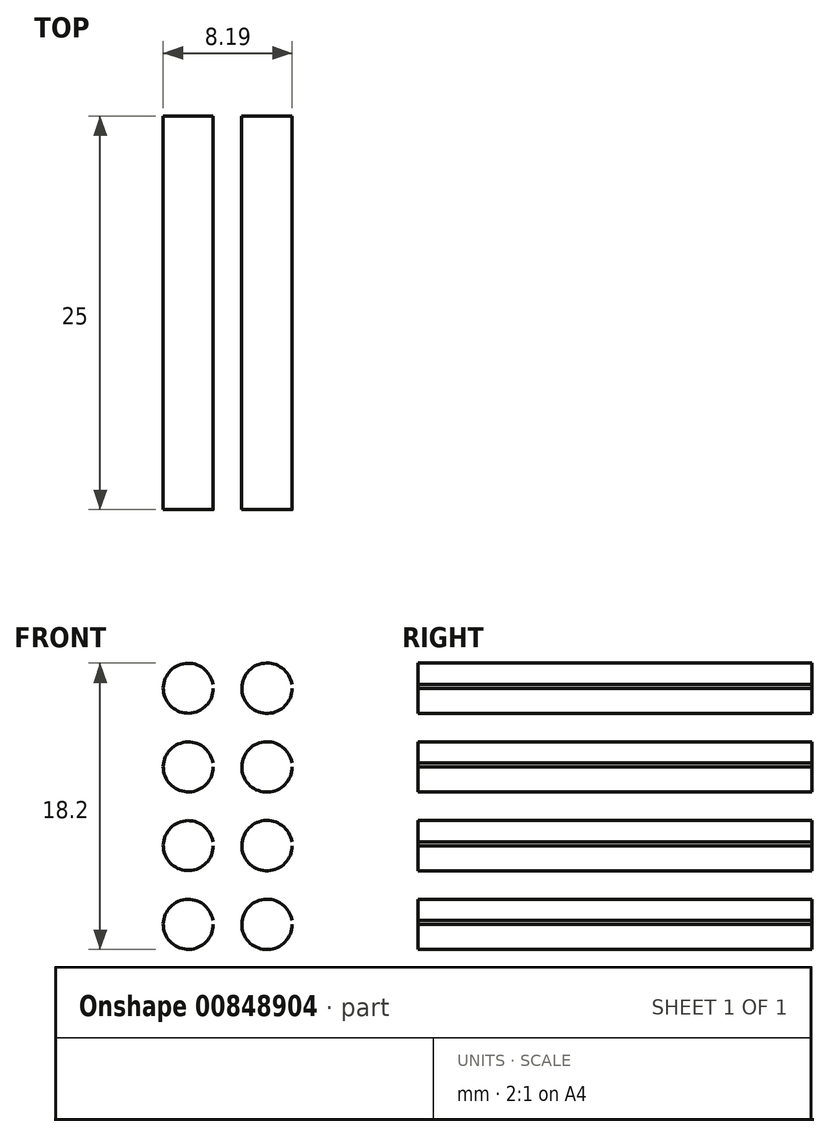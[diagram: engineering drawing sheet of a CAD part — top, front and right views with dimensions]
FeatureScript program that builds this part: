
annotation { "Feature Type Name" : "Feature", "Feature Type Description" : "" }
export const myFeature = defineFeature(function(context is Context, id is Id, definition is map)
    precondition{}
    {
        {
            var Q0;
            Q0=qCreatedBy(makeId("Front.planeOp"),FACE);
            var sketch = newSketch(context, id + "F0", { "sketchPlane" : qUnion([Q0])});
            skArc(sketch, "E0", {"start": v(1.57, 0.25) * mm, "mid": v(-1.58, -0.13) * mm, "end": v(1.59, 0) * mm});
            skLineSegment(sketch, "E1", {"start": v(0, 0) * mm, "end": v(0, 35.3) * mm, "construction": true});
            skLineSegment(sketch, "E2.direction2", {"start": v(0, 0) * mm, "end": v(0, 5) * mm, "construction": true});
            skLineSegment(sketch, "E3", {"start": v(0, 0) * mm, "end": v(0, -5) * mm, "construction": true});
            skLineSegment(sketch, "E4.bottom", {"start": v(0, 0) * mm, "end": v(2, 0) * mm, "construction": true});
            skLineSegment(sketch, "E4.top", {"start": v(0, 0.25) * mm, "end": v(2, 0.25) * mm, "construction": true});
            skLineSegment(sketch, "E4.left", {"start": v(0, 0) * mm, "end": v(0, 0.25) * mm, "construction": true});
            skLineSegment(sketch, "E4.right", {"start": v(2, 0) * mm, "end": v(2, 0.25) * mm, "construction": true});
            skLineSegment(sketch, "E5.0.1.0", {"start": v(0, 5) * mm, "end": v(2, 5) * mm, "construction": true});
            skArc(sketch, "E5.0.1.1", {"start": v(1.57, 5.25) * mm, "mid": v(-1.58, 4.87) * mm, "end": v(1.59, 5) * mm});
            skLineSegment(sketch, "E5.0.1.2", {"start": v(0, 5.25) * mm, "end": v(2, 5.25) * mm, "construction": true});
            skLineSegment(sketch, "E5.0.1.3", {"start": v(2, 5) * mm, "end": v(2, 5.25) * mm, "construction": true});
            skLineSegment(sketch, "E5.0.1.4", {"start": v(0, 5) * mm, "end": v(0, 5.25) * mm, "construction": true});
            skLineSegment(sketch, "E5.0.2.0", {"start": v(0, 10) * mm, "end": v(2, 10) * mm, "construction": true});
            skArc(sketch, "E5.0.2.1", {"start": v(1.57, 10.25) * mm, "mid": v(-1.58, 9.87) * mm, "end": v(1.59, 10) * mm});
            skLineSegment(sketch, "E5.0.2.2", {"start": v(0, 10.25) * mm, "end": v(2, 10.25) * mm, "construction": true});
            skLineSegment(sketch, "E5.0.2.3", {"start": v(2, 10) * mm, "end": v(2, 10.25) * mm, "construction": true});
            skLineSegment(sketch, "E5.0.2.4", {"start": v(0, 10) * mm, "end": v(0, 10.25) * mm, "construction": true});
            skLineSegment(sketch, "E5.0.3.0", {"start": v(0, 15) * mm, "end": v(2, 15) * mm, "construction": true});
            skArc(sketch, "E5.0.3.1", {"start": v(1.57, 15.25) * mm, "mid": v(-1.58, 14.87) * mm, "end": v(1.59, 15) * mm});
            skLineSegment(sketch, "E5.0.3.2", {"start": v(0, 15.25) * mm, "end": v(2, 15.25) * mm, "construction": true});
            skLineSegment(sketch, "E5.0.3.3", {"start": v(2, 15) * mm, "end": v(2, 15.25) * mm, "construction": true});
            skLineSegment(sketch, "E5.0.3.4", {"start": v(0, 15) * mm, "end": v(0, 15.25) * mm, "construction": true});
            skLineSegment(sketch, "E5.direction1", {"start": v(0, 0) * mm, "end": v(25, 0) * mm, "construction": true});
            skArc(sketch, "E6", {"start": v(6.58, 0.25) * mm, "mid": v(3.4, -0.13) * mm, "end": v(6.6, 0) * mm});
            skLineSegment(sketch, "E7.bottom", {"start": v(5, 0) * mm, "end": v(7, 0) * mm, "construction": true});
            skLineSegment(sketch, "E7.top", {"start": v(5, 0.25) * mm, "end": v(7, 0.25) * mm, "construction": true});
            skLineSegment(sketch, "E7.left", {"start": v(5, 0) * mm, "end": v(5, 0.25) * mm, "construction": true});
            skLineSegment(sketch, "E7.right", {"start": v(7, 0) * mm, "end": v(7, 0.25) * mm, "construction": true});
            skLineSegment(sketch, "E8.0.1.0", {"start": v(5, 5.25) * mm, "end": v(7, 5.25) * mm, "construction": true});
            skArc(sketch, "E8.0.1.1", {"start": v(6.58, 5.25) * mm, "mid": v(3.4, 4.87) * mm, "end": v(6.6, 5) * mm});
            skLineSegment(sketch, "E8.0.1.2", {"start": v(5, 5) * mm, "end": v(7, 5) * mm, "construction": true});
            skLineSegment(sketch, "E8.0.1.3", {"start": v(7, 5) * mm, "end": v(7, 5.25) * mm, "construction": true});
            skLineSegment(sketch, "E8.0.1.4", {"start": v(5, 5) * mm, "end": v(5, 5.25) * mm, "construction": true});
            skLineSegment(sketch, "E8.0.2.0", {"start": v(5, 10.25) * mm, "end": v(7, 10.25) * mm, "construction": true});
            skArc(sketch, "E8.0.2.1", {"start": v(6.58, 10.25) * mm, "mid": v(3.4, 9.87) * mm, "end": v(6.6, 10) * mm});
            skLineSegment(sketch, "E8.0.2.2", {"start": v(5, 10) * mm, "end": v(7, 10) * mm, "construction": true});
            skLineSegment(sketch, "E8.0.2.3", {"start": v(7, 10) * mm, "end": v(7, 10.25) * mm, "construction": true});
            skLineSegment(sketch, "E8.0.2.4", {"start": v(5, 10) * mm, "end": v(5, 10.25) * mm, "construction": true});
            skLineSegment(sketch, "E8.0.3.0", {"start": v(5, 15.25) * mm, "end": v(7, 15.25) * mm, "construction": true});
            skArc(sketch, "E8.0.3.1", {"start": v(6.58, 15.25) * mm, "mid": v(3.4, 14.87) * mm, "end": v(6.6, 15) * mm});
            skLineSegment(sketch, "E8.0.3.2", {"start": v(5, 15) * mm, "end": v(7, 15) * mm, "construction": true});
            skLineSegment(sketch, "E8.0.3.3", {"start": v(7, 15) * mm, "end": v(7, 15.25) * mm, "construction": true});
            skLineSegment(sketch, "E8.0.3.4", {"start": v(5, 15) * mm, "end": v(5, 15.25) * mm, "construction": true});
            skLineSegment(sketch, "E8.direction1", {"start": v(5, 0) * mm, "end": v(30, 0) * mm, "construction": true});
            skLineSegment(sketch, "E8.direction2", {"start": v(5, 0) * mm, "end": v(5, 5) * mm, "construction": true});
            skSolve(sketch);
        }
        {
            var Q0;
            Q0 = qSketchRegion(id + "F0", true);
            var Q1;
            Q1=sQuery(id+"F0.wireOp",EDGE,"E0");
            var Q2;
            Q2=sQuery(id+"F0.wireOp",EDGE,"E8.0.1.1");
            var Q3;
            Q3=sQuery(id+"F0.wireOp",EDGE,"E6");
            var Q4;
            Q4=sQuery(id+"F0.wireOp",EDGE,"E5.0.1.1");
            var Q5;
            Q5=sQuery(id+"F0.wireOp",EDGE,"E5.0.2.1");
            var Q6;
            Q6=sQuery(id+"F0.wireOp",EDGE,"E8.0.2.1");
            var Q7;
            Q7=sQuery(id+"F0.wireOp",EDGE,"E8.0.3.1");
            var Q8;
            Q8=sQuery(id+"F0.wireOp",EDGE,"E5.0.3.1");
            extrude(context, id + "F1", {"entities" : qUnion([Q0]), "bodyType" : ToolBodyType.SURFACE, "surfaceEntities" : qUnion([Q1, Q2, Q3, Q4, Q5, Q6, Q7, Q8]), "depth" : 25 * mm, "offsetDistance" : 25 * mm});
        }
    });
